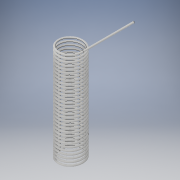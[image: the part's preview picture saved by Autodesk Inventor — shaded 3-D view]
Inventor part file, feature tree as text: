
AUTODESK INVENTOR PART (.ipt)
format: ipt  version: 2018 (Build 220112000, 112)  size: 515,072 bytes
history: native  units: in
note: dims shown in document units (in); Inventor stores cm internally (conversion verified against a paired STEP export)
features: sketch x3, extrude x2, helix x1
ambient origin geometry x8: Origin, YZ Plane, XZ Plane, XY Plane, X Axis, Y Axis, Z Axis, Center Point
bodies: Solid1 (feature_tree)
feature tree (6):
  helix  "Coil1"  [1 undecoded]
  extrude  "Extrusion1"  Depth=0.35in TaperAngle=0.0deg
  extrude  "Extrusion2"  [1 undecoded]
  sketch  "Sketch1"  dims[d1=0.0875in]
  sketch  "Sketch2"  dims[d2=1.0in d3=0.67in d4=12.0079in d5=0.0in d6=90.0deg d7=90.0deg d8=0.0in d9=0.0in d10=0.35in d11=0.0in]
  sketch  "Sketch3"  dims[d12=0.2in d13=0.0in]
note: 2 required parameter values undecoded (feature->parameter linkage not recoverable at this tier; creation-order binding heuristic only, values carry confidence <= 0.55)
